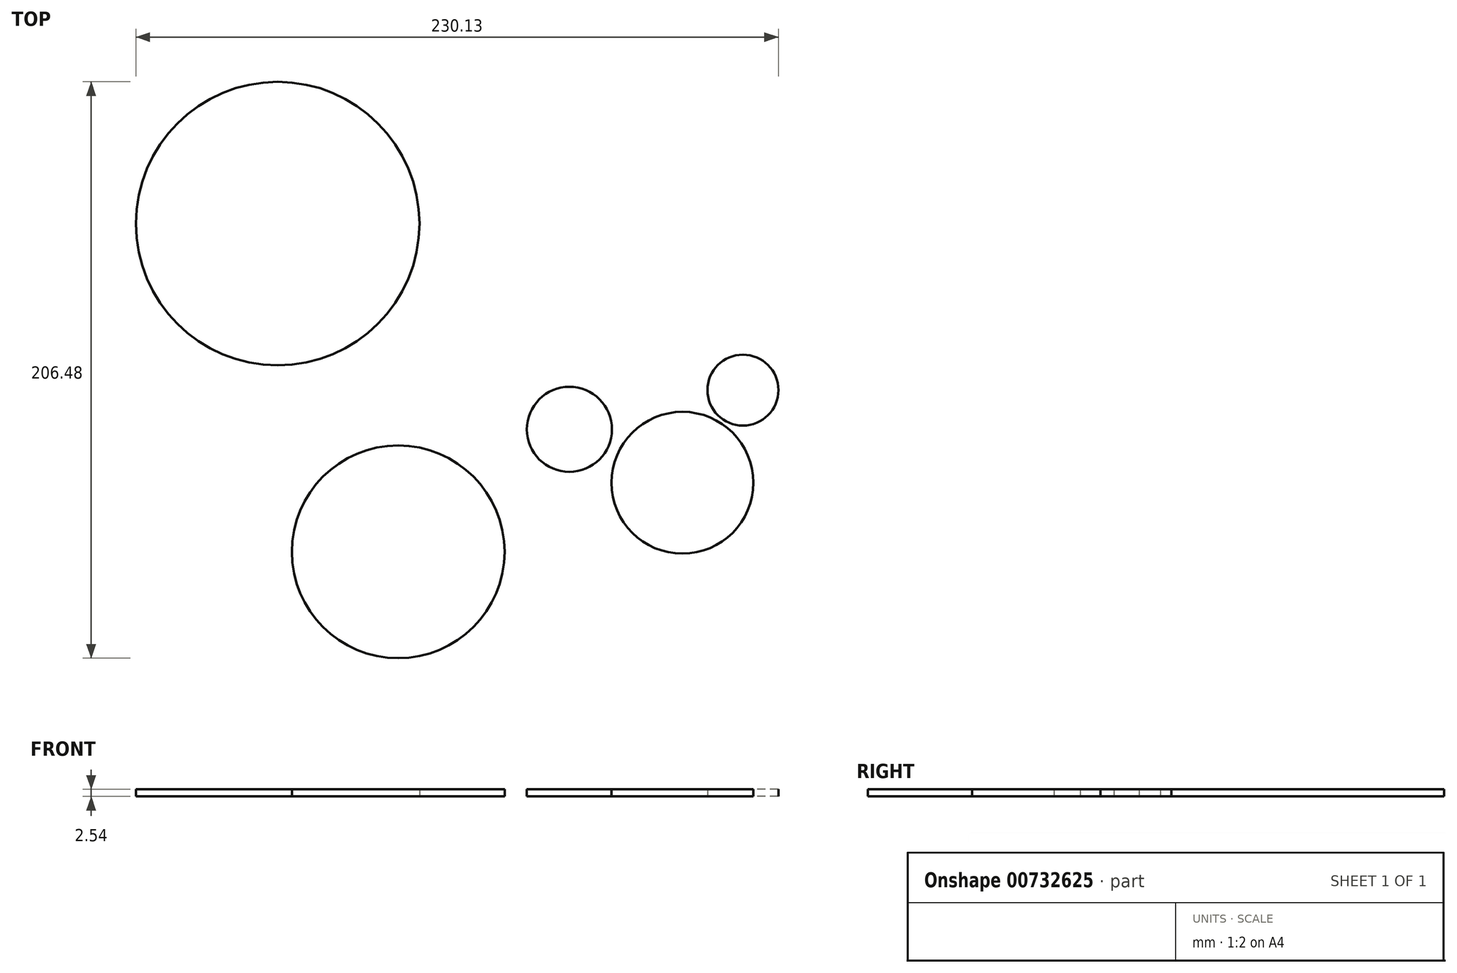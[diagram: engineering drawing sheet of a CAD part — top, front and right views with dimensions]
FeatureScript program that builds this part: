
annotation { "Feature Type Name" : "Feature", "Feature Type Description" : "" }
export const myFeature = defineFeature(function(context is Context, id is Id, definition is map)
    precondition{}
    {
        {
            var Q0;
            Q0=qCreatedBy(makeId("Top.planeOp"),FACE);
            var sketch = newSketch(context, id + "F0", { "sketchPlane" : qUnion([Q0])});
            skCircle(sketch, "E0", {"center": v(55.82, 50.06) * mm, "radius": 12.7 * mm});
            skCircle(sketch, "E1", {"center": v(-6.33, 36) * mm, "radius": 15.24 * mm});
            skCircle(sketch, "E2", {"center": v(34.17, 16.87) * mm, "radius": 25.4 * mm});
            skCircle(sketch, "E3", {"center": v(-67.64, -7.87) * mm, "radius": 38.1 * mm});
            skCircle(sketch, "E4", {"center": v(-110.8, 109.7) * mm, "radius": 50.8 * mm});
            skSolve(sketch);
        }
        {
            var Q0;
            Q0=makeQuery(id+"F0.imprint","IMPRINT",FACE,{"disambiguationData":[TD([[makeQuery(id+"F0.imprint","IMPRINT",EDGE,{"derivedFrom":sQuery(id+"F0.wireOp",EDGE,"E4")}),1.0]])]});
            extrude(context, id + "F1", {"entities" : qUnion([Q0]), "depth" : 2.54 * mm, "offsetDistance" : 25.4 * mm});
        }
        {
            var Q0;
            Q0=makeQuery(id+"F0.imprint","IMPRINT",FACE,{"disambiguationData":[TD([[makeQuery(id+"F0.imprint","IMPRINT",EDGE,{"derivedFrom":sQuery(id+"F0.wireOp",EDGE,"E3")}),1.0]])]});
            var Q1;
            Q1=makeQuery(id+"F0.imprint","IMPRINT",FACE,{"disambiguationData":[TD([[makeQuery(id+"F0.imprint","IMPRINT",EDGE,{"derivedFrom":sQuery(id+"F0.wireOp",EDGE,"E1")}),1.0]])]});
            var Q2;
            Q2=makeQuery(id+"F0.imprint","IMPRINT",FACE,{"disambiguationData":[TD([[makeQuery(id+"F0.imprint","IMPRINT",EDGE,{"derivedFrom":sQuery(id+"F0.wireOp",EDGE,"E2")}),1.0]])]});
            var Q3;
            Q3=makeQuery(id+"F0.imprint","IMPRINT",FACE,{"disambiguationData":[TD([[makeQuery(id+"F0.imprint","IMPRINT",EDGE,{"derivedFrom":sQuery(id+"F0.wireOp",EDGE,"E0")}),1.0]])]});
            extrude(context, id + "F2", {"entities" : qUnion([Q0, Q1, Q2, Q3]), "depth" : 2.54 * mm, "offsetDistance" : 25.4 * mm});
        }
    });
